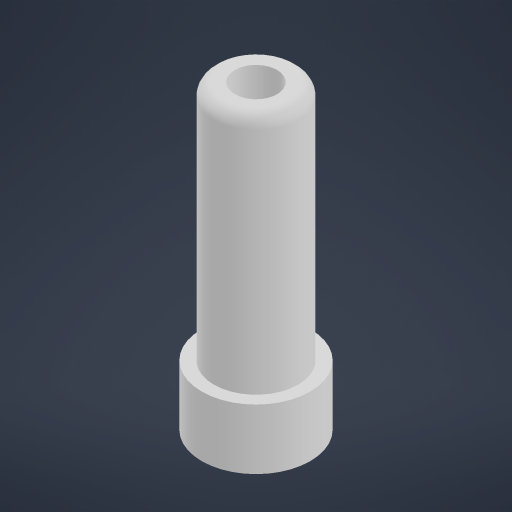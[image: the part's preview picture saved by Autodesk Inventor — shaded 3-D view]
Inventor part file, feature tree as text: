
AUTODESK INVENTOR PART (.ipt)
format: ipt  version: 2024.1 (Build 281209000, 209)  size: 181,248 bytes
history: native  units: mm
features: extrude x2, sketch x1, fillet x1
ambient origin geometry x8: Origin, YZ Plane, XZ Plane, XY Plane, X Axis, Y Axis, Z Axis, Center Point
bodies: Body1 (feature_tree)
feature tree (4):
  sketch  "Sketch5"  dims[d43=9.0mm d44=4.5mm d45=3.5mm d46=7.0mm d47=5.0mm d48=0.0mm d49=20.0mm d50=0.0mm d51=1.0mm]
  extrude  "Extrusion9"  Depth=4.5mm
  extrude  "Extrusion10"  Depth=3.5mm
  fillet  "Fillet3"  Radius=7.0mm
